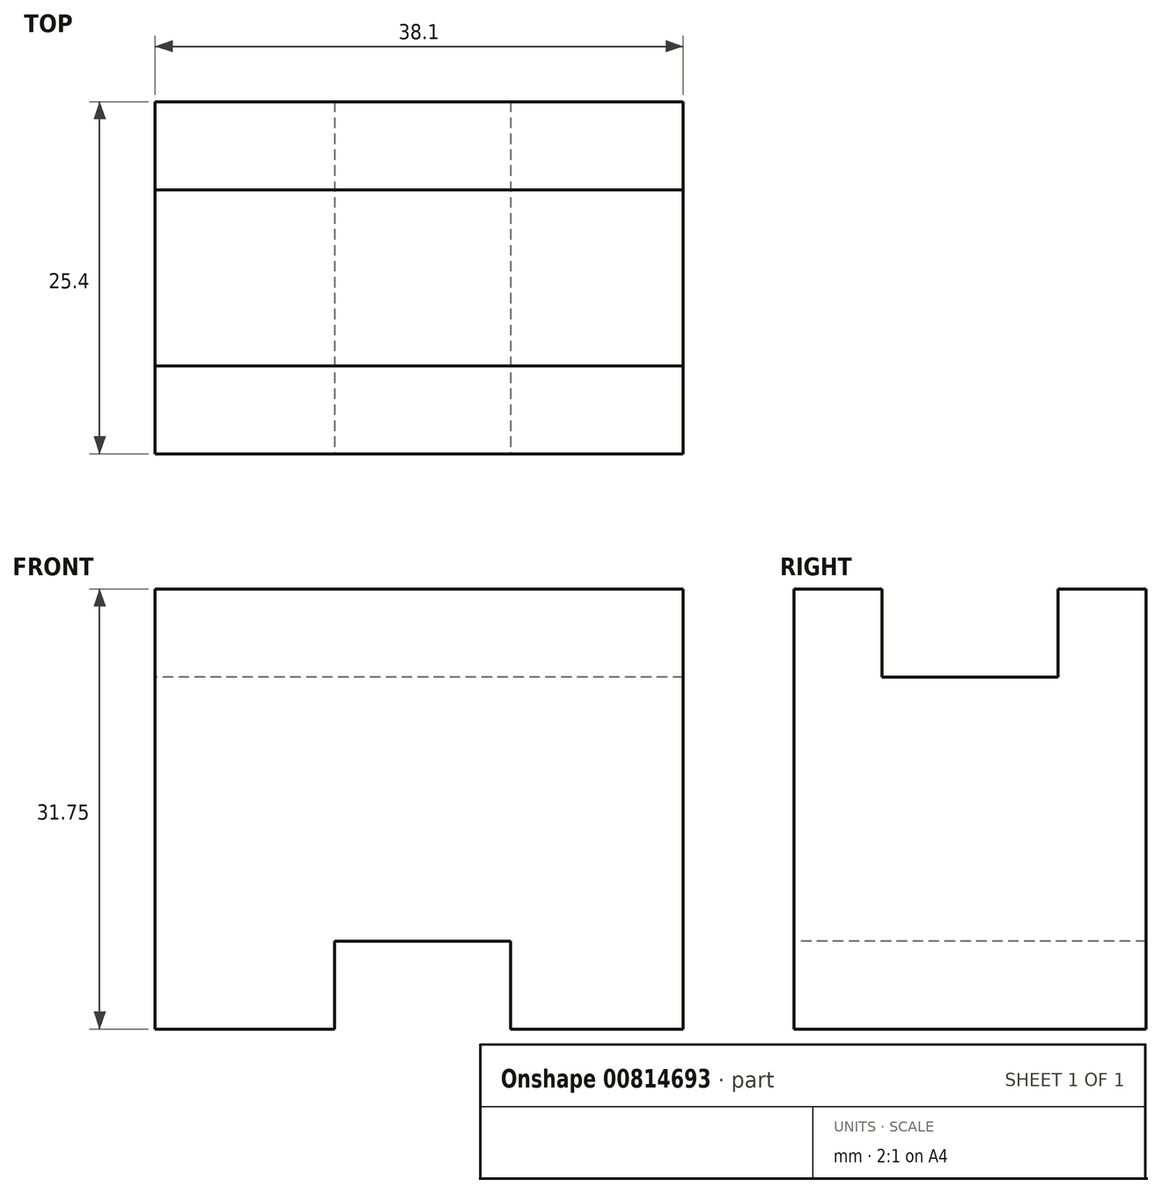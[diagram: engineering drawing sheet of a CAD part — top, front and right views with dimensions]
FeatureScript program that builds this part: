
annotation { "Feature Type Name" : "Feature", "Feature Type Description" : "" }
export const myFeature = defineFeature(function(context is Context, id is Id, definition is map)
    precondition{}
    {
        {
            var Q0;
            Q0=qCreatedBy(makeId("Right.planeOp"),FACE);
            var sketch = newSketch(context, id + "F0", { "sketchPlane" : qUnion([Q0])});
            skLineSegment(sketch, "E0", {"start": v(0, 0) * mm, "end": v(0, 31.75) * mm});
            skLineSegment(sketch, "E1", {"start": v(0, 31.75) * mm, "end": v(6.35, 31.75) * mm});
            skLineSegment(sketch, "E2", {"start": v(6.35, 31.75) * mm, "end": v(6.35, 25.4) * mm});
            skLineSegment(sketch, "E3", {"start": v(6.35, 25.4) * mm, "end": v(19.05, 25.4) * mm});
            skLineSegment(sketch, "E4", {"start": v(19.05, 25.4) * mm, "end": v(19.05, 31.75) * mm});
            skLineSegment(sketch, "E5", {"start": v(19.05, 31.75) * mm, "end": v(25.4, 31.75) * mm});
            skLineSegment(sketch, "E6", {"start": v(25.4, 31.75) * mm, "end": v(25.4, 0) * mm});
            skLineSegment(sketch, "E7", {"start": v(25.4, 0) * mm, "end": v(0, 0) * mm});
            skSolve(sketch);
        }
        {
            var Q0;
            Q0=makeQuery(id+"F0.imprint","IMPRINT",FACE,{"disambiguationData":[TD([[makeQuery(id+"F0.imprint","IMPRINT",EDGE,{"derivedFrom":sQuery(id+"F0.wireOp",EDGE,"E0")}),-1.0]])]});
            extrude(context, id + "F1", {"entities" : qUnion([Q0]), "depth" : 38.1 * mm, "offsetDistance" : 25.4 * mm});
        }
        {
            var Q0;
            Q0=makeQuery(id+"F1.opExtrude","SWEPT_FACE",FACE,{"disambiguationData":[OSD([sQuery(id+"F0.wireOp",EDGE,"E0")])]});
            var sketch = newSketch(context, id + "F2", { "sketchPlane" : qUnion([Q0])});
            skLineSegment(sketch, "E8", {"start": v(12.95, 0) * mm, "end": v(25.65, 0) * mm});
            skLineSegment(sketch, "E9", {"start": v(25.65, 0) * mm, "end": v(25.65, 6.35) * mm});
            skLineSegment(sketch, "E10", {"start": v(25.65, 6.35) * mm, "end": v(12.95, 6.35) * mm});
            skLineSegment(sketch, "E11", {"start": v(12.95, 6.35) * mm, "end": v(12.95, 0) * mm});
            skSolve(sketch);
        }
        {
            var Q0;
            Q0=makeQuery(id+"F2.imprint","IMPRINT",FACE,{"disambiguationData":[TD([[makeQuery(id+"F2.imprint","IMPRINT",EDGE,{"derivedFrom":sQuery(id+"F2.wireOp",EDGE,"E8")}),-1.0]])]});
            extrude(context, id + "F3", {"entities" : qUnion([Q0]), "operationType" : NewBodyOperationType.REMOVE, "oppositeDirection" : true, "depth" : 25.4 * mm, "offsetDistance" : 25.4 * mm});
        }
    });
